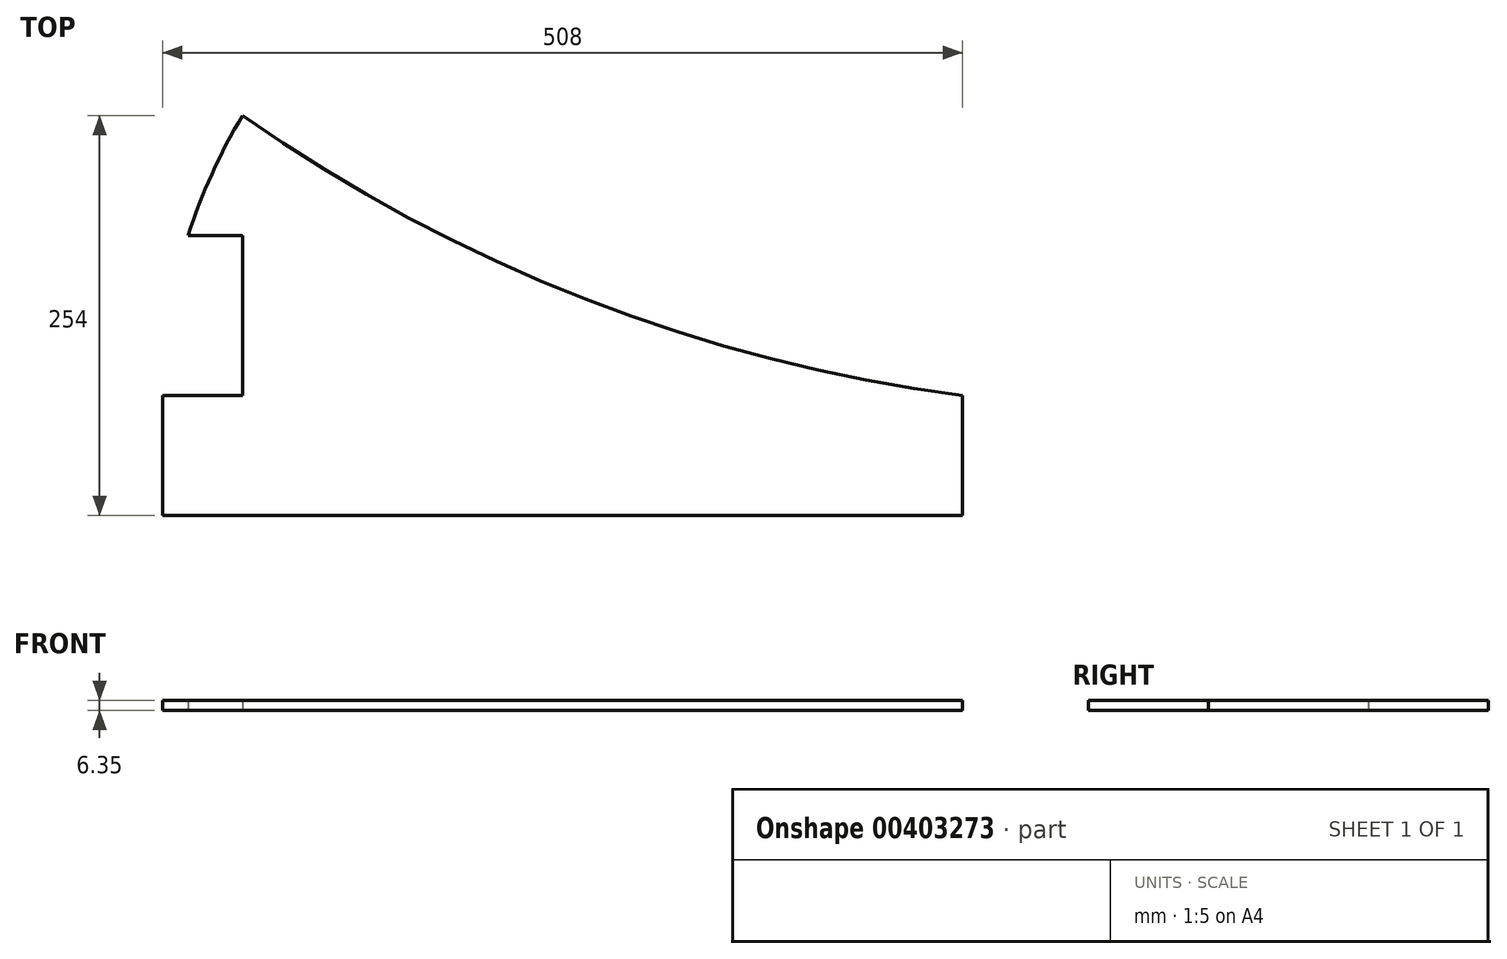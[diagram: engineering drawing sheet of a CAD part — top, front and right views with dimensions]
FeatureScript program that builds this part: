
annotation { "Feature Type Name" : "Feature", "Feature Type Description" : "" }
export const myFeature = defineFeature(function(context is Context, id is Id, definition is map)
    precondition{}
    {
        {
            var Q0;
            Q0=qCreatedBy(makeId("Top.planeOp"),FACE);
            var sketch = newSketch(context, id + "F0", { "sketchPlane" : qUnion([Q0])});
            skLineSegment(sketch, "E0.bottom", {"start": v(0, 0) * mm, "end": v(50.8, 0) * mm});
            skLineSegment(sketch, "E0.top", {"start": v(0, 177.8) * mm, "end": v(50.8, 177.8) * mm});
            skLineSegment(sketch, "E0.left", {"start": v(0, 0) * mm, "end": v(0, 177.8) * mm});
            skLineSegment(sketch, "E0.right", {"start": v(50.8, 0) * mm, "end": v(50.8, 177.8) * mm});
            skLineSegment(sketch, "E1.bottom", {"start": v(0, 0) * mm, "end": v(25.4, 0) * mm});
            skLineSegment(sketch, "E1.top", {"start": v(0, 127) * mm, "end": v(25.4, 127) * mm});
            skLineSegment(sketch, "E1.left", {"start": v(0, 0) * mm, "end": v(0, 127) * mm});
            skLineSegment(sketch, "E1.right", {"start": v(25.4, 0) * mm, "end": v(25.4, 127) * mm});
            skLineSegment(sketch, "E2.bottom", {"start": v(0, 0) * mm, "end": v(48.4, 0) * mm});
            skLineSegment(sketch, "E3.bottom", {"start": v(0, 0) * mm, "end": v(177.8, 0) * mm});
            skLineSegment(sketch, "E3.top", {"start": v(0, 101.6) * mm, "end": v(177.8, 101.6) * mm});
            skLineSegment(sketch, "E3.left", {"start": v(0, 0) * mm, "end": v(0, 101.6) * mm});
            skLineSegment(sketch, "E3.right", {"start": v(177.8, 0) * mm, "end": v(177.8, 101.6) * mm});
            skLineSegment(sketch, "E4", {"start": v(0, 0) * mm, "end": v(508, 0) * mm});
            skCircle(sketch, "E5", {"center": v(639.68, 1015.33) * mm, "radius": 1023.83 * mm});
            skCircle(sketch, "E6", {"center": v(351.37, -4.23) * mm, "radius": 351.4 * mm});
            skLineSegment(sketch, "E7.bottom", {"start": v(508, 0) * mm, "end": v(0, 0) * mm});
            skLineSegment(sketch, "E7.top", {"start": v(508, -76.2) * mm, "end": v(0, -76.2) * mm});
            skLineSegment(sketch, "E7.left", {"start": v(508, 0) * mm, "end": v(508, -76.2) * mm});
            skLineSegment(sketch, "E7.right", {"start": v(0, 0) * mm, "end": v(0, -76.2) * mm});
            skSolve(sketch);
        }
        {
            var Q0;
            {var subQ0=sQuery(id+"F0.wireOp",EDGE,"E4");var subQ1=sQuery(id+"F0.wireOp",EDGE,"E1.right");var subQ2=makeQuery(id+"F0.imprint","INTERSECT",VERTEX,{"derivedFrom":[subQ1,subQ0]});Q0=makeQuery(id+"F0.imprint","IMPRINT",FACE,{"disambiguationData":[TD([[makeQuery(id+"F0.imprint","IMPRINT",EDGE,{"disambiguationData":[TD([[subQ2,-1.0]])],"derivedFrom":subQ1}),1.0]])]});}
            var Q1;
            {var subQ1=sQuery(id+"F0.wireOp",EDGE,"E1.right");var subQ3=sQuery(id+"F0.wireOp",EDGE,"E3.top");var subQ4=makeQuery(id+"F0.imprint","INTERSECT",VERTEX,{"derivedFrom":[subQ1,subQ3]});Q1=makeQuery(id+"F0.imprint","IMPRINT",FACE,{"disambiguationData":[TD([[makeQuery(id+"F0.imprint","IMPRINT",EDGE,{"disambiguationData":[TD([[subQ4,1.0]])],"derivedFrom":subQ3}),1.0]])]});}
            var Q2;
            {var subQ1=sQuery(id+"F0.wireOp",EDGE,"E0.right");var subQ3=sQuery(id+"F0.wireOp",EDGE,"E3.top");var subQ4=makeQuery(id+"F0.imprint","INTERSECT",VERTEX,{"derivedFrom":[subQ1,subQ3]});Q2=makeQuery(id+"F0.imprint","IMPRINT",FACE,{"disambiguationData":[TD([[makeQuery(id+"F0.imprint","IMPRINT",EDGE,{"disambiguationData":[TD([[subQ4,1.0]])],"derivedFrom":subQ3}),1.0]])]});}
            var Q3;
            {var subQ1=sQuery(id+"F0.wireOp",EDGE,"E0.right");var subQ3=sQuery(id+"F0.wireOp",EDGE,"E3.top");var subQ4=makeQuery(id+"F0.imprint","INTERSECT",VERTEX,{"derivedFrom":[subQ1,subQ3]});Q3=makeQuery(id+"F0.imprint","IMPRINT",FACE,{"disambiguationData":[TD([[makeQuery(id+"F0.imprint","IMPRINT",EDGE,{"disambiguationData":[TD([[subQ4,-1.0]])],"derivedFrom":subQ3}),1.0]])]});}
            var Q4;
            {var subQ5=sQuery(id+"F0.wireOp",EDGE,"E3.right");Q4=makeQuery(id+"F0.imprint","IMPRINT",FACE,{"disambiguationData":[TD([[makeQuery(id+"F0.imprint","IMPRINT",EDGE,{"derivedFrom":subQ5}),1.0]])]});}
            var Q5;
            {var subQ0=sQuery(id+"F0.wireOp",EDGE,"E4");var subQ3=makeQuery(id+"F0.imprint","IMPRINT",VERTEX,{"derivedFrom":subQ0});Q5=makeQuery(id+"F0.imprint","IMPRINT",FACE,{"disambiguationData":[TD([[makeQuery(id+"F0.imprint","IMPRINT",EDGE,{"disambiguationData":[TD([[subQ3,1.0]])],"derivedFrom":subQ0}),1.0]])]});}
            var Q6;
            {var subQ0=sQuery(id+"F0.wireOp",EDGE,"E3.right");Q6=makeQuery(id+"F0.imprint","IMPRINT",FACE,{"disambiguationData":[TD([[makeQuery(id+"F0.imprint","IMPRINT",EDGE,{"derivedFrom":subQ0}),-1.0]])]});}
            var Q7;
            {var subQ5=sQuery(id+"F0.wireOp",EDGE,"E7.bottom");var subQ7=makeQuery(id+"F0.imprint","IMPRINT",VERTEX,{"derivedFrom":subQ5});Q7=makeQuery(id+"F0.imprint","IMPRINT",FACE,{"disambiguationData":[TD([[makeQuery(id+"F0.imprint","IMPRINT",EDGE,{"disambiguationData":[TD([[subQ7,1.0]])],"derivedFrom":subQ5}),-1.0]])]});}
            var Q8;
            {var subQ0=sQuery(id+"F0.wireOp",EDGE,"E7.bottom");var subQ1=sQuery(id+"F0.wireOp",EDGE,"E1.right");var subQ2=makeQuery(id+"F0.imprint","INTERSECT",VERTEX,{"derivedFrom":[subQ1,subQ0]});Q8=makeQuery(id+"F0.imprint","IMPRINT",FACE,{"disambiguationData":[TD([[makeQuery(id+"F0.imprint","IMPRINT",EDGE,{"disambiguationData":[TD([[subQ2,-1.0]])],"derivedFrom":subQ1}),1.0]])]});}
            var Q9;
            {var subQ3=sQuery(id+"F0.wireOp",EDGE,"E7.left");Q9=makeQuery(id+"F0.imprint","IMPRINT",FACE,{"disambiguationData":[TD([[makeQuery(id+"F0.imprint","IMPRINT",EDGE,{"derivedFrom":subQ3}),-1.0]])]});}
            var Q10;
            {var subQ0=sQuery(id+"F0.wireOp",EDGE,"E7.right");var subQ1=sQuery(id+"F0.wireOp",EDGE,"E6");var subQ2=makeQuery(id+"F0.imprint","INTERSECT",VERTEX,{"derivedFrom":[subQ1,subQ0]});Q10=makeQuery(id+"F0.imprint","IMPRINT",FACE,{"disambiguationData":[TD([[makeQuery(id+"F0.imprint","IMPRINT",EDGE,{"disambiguationData":[TD([[subQ2,-1.0]])],"derivedFrom":subQ1}),-1.0]])]});}
            extrude(context, id + "F1", {"entities" : qUnion([Q0, Q1, Q2, Q3, Q4, Q5, Q6, Q7, Q8, Q9, Q10]), "depth" : 6.35 * mm});
        }
    });
